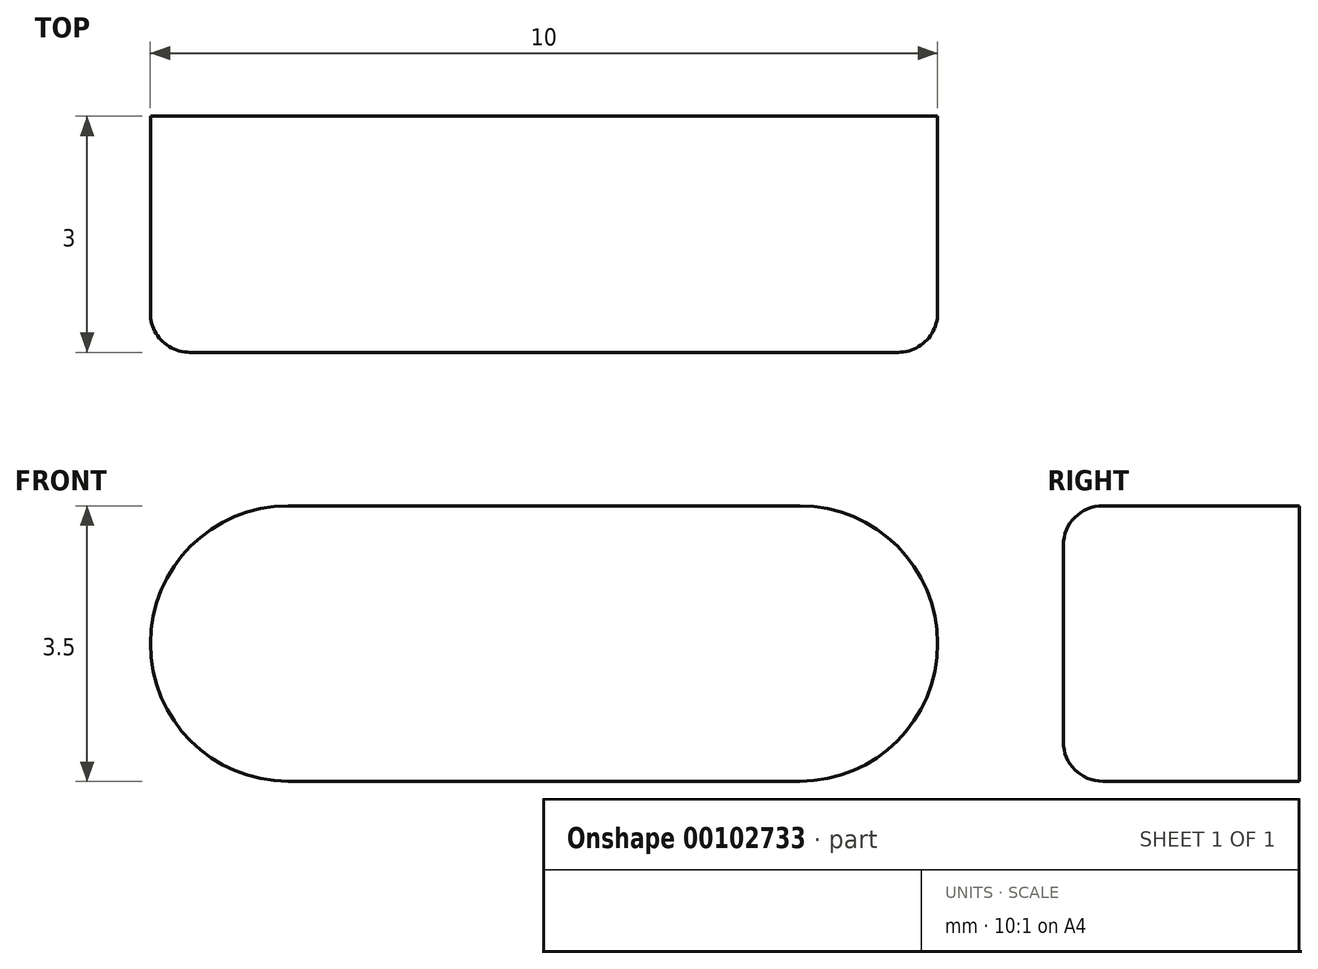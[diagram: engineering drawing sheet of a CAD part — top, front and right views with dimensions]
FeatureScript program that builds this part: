
annotation { "Feature Type Name" : "Feature", "Feature Type Description" : "" }
export const myFeature = defineFeature(function(context is Context, id is Id, definition is map)
    precondition{}
    {
        {
            var Q0;
            Q0=qCreatedBy(makeId("Front.planeOp"),FACE);
            var sketch = newSketch(context, id + "F0", { "sketchPlane" : qUnion([Q0])});
            skArc(sketch, "E0", {"start": v(-10.15, 1.75) * mm, "mid": v(-11.9, 0) * mm, "end": v(-10.15, -1.75) * mm});
            skArc(sketch, "E1", {"start": v(-3.65, -1.75) * mm, "mid": v(-1.9, 0) * mm, "end": v(-3.65, 1.75) * mm});
            skLineSegment(sketch, "E2", {"start": v(-10.15, 1.75) * mm, "end": v(-3.65, 1.75) * mm});
            skLineSegment(sketch, "E3", {"start": v(-10.15, -1.75) * mm, "end": v(-3.65, -1.75) * mm});
            skSolve(sketch);
        }
        {
            var Q0;
            Q0=makeQuery(id+"F0.imprint","IMPRINT",FACE,{"disambiguationData":[TD([[makeQuery(id+"F0.imprint","IMPRINT",EDGE,{"derivedFrom":sQuery(id+"F0.wireOp",EDGE,"E0")}),1.0]])]});
            extrude(context, id + "F1", {"entities" : qUnion([Q0]), "depth" : 3 * mm});
        }
        {
            var Q0;
            Q0=makeQuery(id+"F1.opExtrude","CAP_EDGE",EDGE,{"disambiguationData":[OSD([sQuery(id+"F0.wireOp",EDGE,"E2")])],"isStart":false});
            var Q1;
            Q1=makeQuery(id+"F1.opExtrude","CAP_EDGE",EDGE,{"disambiguationData":[OSD([sQuery(id+"F0.wireOp",EDGE,"E1")])],"isStart":false});
            var Q2;
            Q2=makeQuery(id+"F1.opExtrude","CAP_EDGE",EDGE,{"disambiguationData":[OSD([sQuery(id+"F0.wireOp",EDGE,"E3")])],"isStart":false});
            var Q3;
            Q3=makeQuery(id+"F1.opExtrude","CAP_EDGE",EDGE,{"disambiguationData":[OSD([sQuery(id+"F0.wireOp",EDGE,"E0")])],"isStart":false});
            fillet(context, id + "F2", {"entities" : qUnion([Q0, Q1, Q2, Q3]), "radius" : 0.5 * mm, "tangentPropagation" : true, "allowEdgeOverflow" : false});
        }
    });
